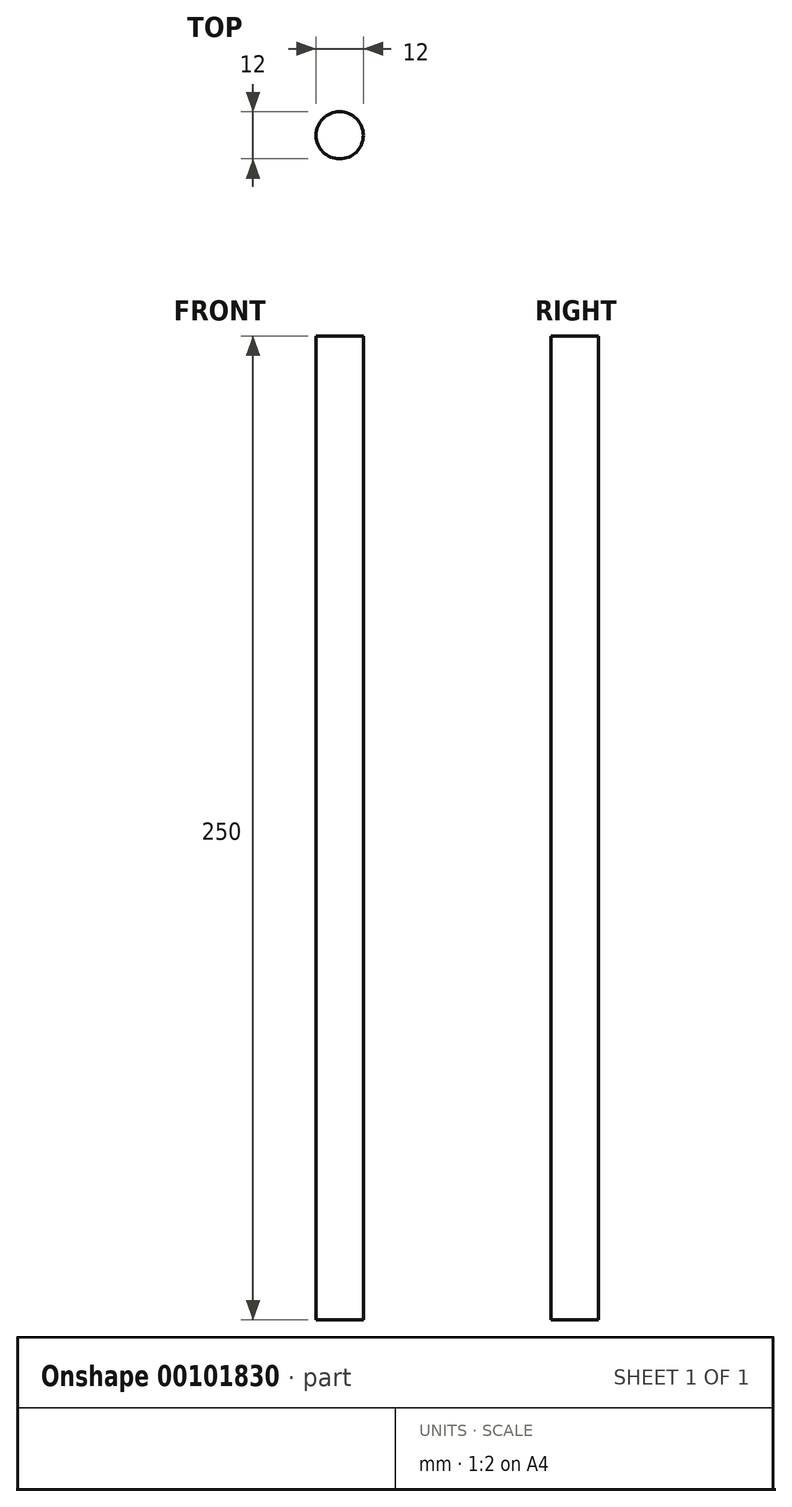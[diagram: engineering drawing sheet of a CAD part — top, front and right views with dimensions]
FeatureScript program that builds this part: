
annotation { "Feature Type Name" : "Feature", "Feature Type Description" : "" }
export const myFeature = defineFeature(function(context is Context, id is Id, definition is map)
    precondition{}
    {
        {
            var Q0;
            Q0=qCreatedBy(makeId("Top.planeOp"),FACE);
            var sketch = newSketch(context, id + "F0", { "sketchPlane" : qUnion([Q0])});
            skCircle(sketch, "E0", {"center": v(0, 0) * mm, "radius": 6 * mm});
            skSolve(sketch);
        }
        {
            var Q0;
            Q0 = qSketchRegion(id + "F0", true);
            extrude(context, id + "F1", {"entities" : qUnion([Q0]), "depth" : 250 * mm});
        }
    });
